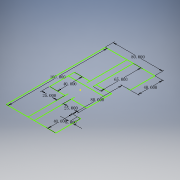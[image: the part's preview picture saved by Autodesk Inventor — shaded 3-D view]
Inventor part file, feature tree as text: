
AUTODESK INVENTOR PART (.ipt)
format: ipt  version: 2018 (Build 220112000, 112)  size: 99,328 bytes
history: native  units: in
note: dims shown in document units (in); Inventor stores cm internally (conversion verified against a paired STEP export)
features: sketch x1
ambient origin geometry x8: Origin, YZ Plane, XZ Plane, XY Plane, X Axis, Y Axis, Z Axis, Center Point
feature tree (1):
  sketch  "草图1"  dims[d2=160.0in d3=80.0in d4=40.0in d5=80.0in d6=40.0in d7=5.0in d11=40.0in d12=25.0in d14=25.0in d16=65.0in]
